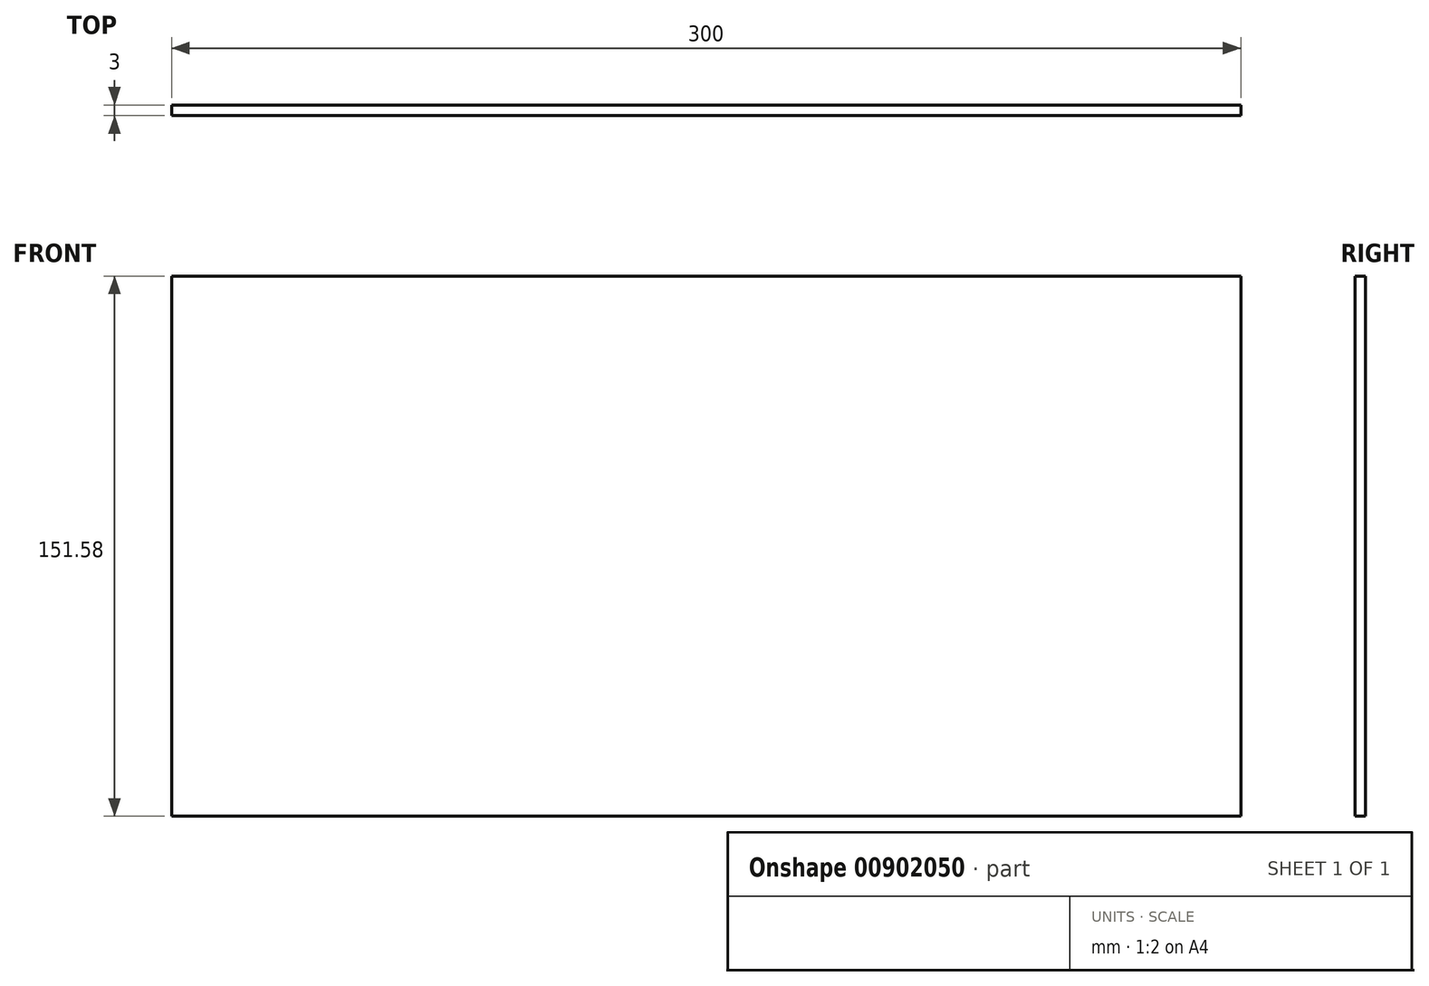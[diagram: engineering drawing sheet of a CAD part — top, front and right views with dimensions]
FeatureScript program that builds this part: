
annotation { "Feature Type Name" : "Feature", "Feature Type Description" : "" }
export const myFeature = defineFeature(function(context is Context, id is Id, definition is map)
    precondition{}
    {
        {
            var Q0;
            Q0=qCreatedBy(makeId("Front.planeOp"),FACE);
            var sketch = newSketch(context, id + "F0", { "sketchPlane" : qUnion([Q0])});
            skLineSegment(sketch, "E0.bottom", {"start": v(150, 75.8) * mm, "end": v(-150, 75.8) * mm});
            skLineSegment(sketch, "E0.top", {"start": v(150, -75.8) * mm, "end": v(-150, -75.8) * mm});
            skLineSegment(sketch, "E0.left", {"start": v(150, 75.8) * mm, "end": v(150, -75.8) * mm});
            skLineSegment(sketch, "E0.right", {"start": v(-150, 75.8) * mm, "end": v(-150, -75.8) * mm});
            skPoint(sketch, "E0.middle", {"position": v(0, 0) * mm});
            skSolve(sketch);
        }
        {
            var Q0;
            Q0 = qSketchRegion(id + "F0", true);
            extrude(context, id + "F1", {"entities" : qUnion([Q0]), "depth" : 3 * mm, "offsetDistance" : 25 * mm});
        }
    });
